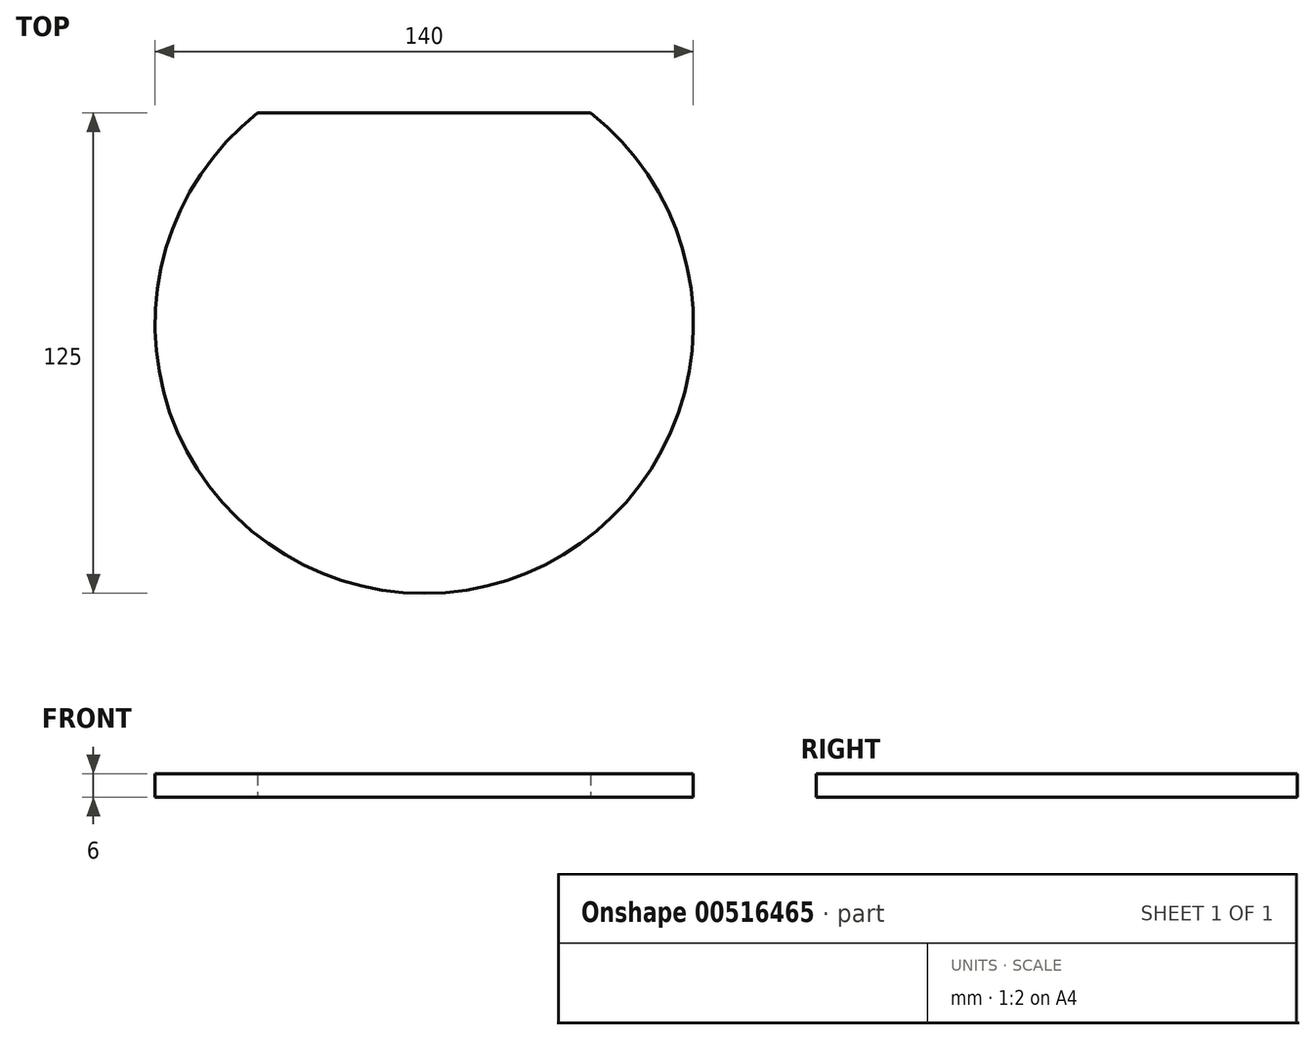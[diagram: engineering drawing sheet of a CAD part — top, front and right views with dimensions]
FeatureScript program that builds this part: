
annotation { "Feature Type Name" : "Feature", "Feature Type Description" : "" }
export const myFeature = defineFeature(function(context is Context, id is Id, definition is map)
    precondition{}
    {
        {
            var Q0;
            Q0=qCreatedBy(makeId("Top.planeOp"),FACE);
            var sketch = newSketch(context, id + "F0", { "sketchPlane" : qUnion([Q0])});
            skCircle(sketch, "E0", {"center": v(0, 0) * mm, "radius": 70 * mm});
            skSolve(sketch);
        }
        {
            var Q0;
            Q0=makeQuery(id+"F0.imprint","IMPRINT",FACE,{"disambiguationData":[TD([[makeQuery(id+"F0.imprint","IMPRINT",EDGE,{"derivedFrom":sQuery(id+"F0.wireOp",EDGE,"E0")}),1.0]])]});
            extrude(context, id + "F1", {"entities" : qUnion([Q0]), "oppositeDirection" : true, "depth" : 6 * mm, "offsetDistance" : 25 * mm});
        }
        {
            var Q0;
            Q0=makeQuery(id+"F1.opExtrude","CAP_FACE",FACE,{"disambiguationData":[OSD([sQuery(id+"F0.wireOp",EDGE,"E0")])],"isStart":true});
            var sketch = newSketch(context, id + "F2", { "sketchPlane" : qUnion([Q0])});
            skLineSegment(sketch, "E1", {"start": v(70, 0) * mm, "end": v(-70, 0) * mm});
            skLineSegment(sketch, "E2", {"start": v(-70, 0) * mm, "end": v(-35, 0) * mm});
            skCircle(sketch, "E3", {"center": v(-35, 0) * mm, "radius": 7 * mm});
            skSolve(sketch);
        }
        {
            var Q0;
            Q0=makeQuery(id+"F1.opExtrude","CAP_FACE",FACE,{"disambiguationData":[OSD([sQuery(id+"F0.wireOp",EDGE,"E0")])],"isStart":false});
            var sketch = newSketch(context, id + "F3", { "sketchPlane" : qUnion([Q0])});
            skLineSegment(sketch, "E4", {"start": v(0, 0) * mm, "end": v(0, -55) * mm});
            skLineSegment(sketch, "E5", {"start": v(0, -55) * mm, "end": v(-43.3, -55) * mm});
            skLineSegment(sketch, "E6", {"start": v(-43.3, -55) * mm, "end": v(43.3, -55) * mm});
            skSolve(sketch);
        }
        {
            var Q0;
            {var subQ0=sQuery(id+"F3.wireOp",EDGE,"E6");var subQ1=makeQuery(id+"F3.imprint","IMPRINT",VERTEX,{"derivedFrom":subQ0});Q0=makeQuery(id+"F3.imprint","IMPRINT",FACE,{"disambiguationData":[TD([[makeQuery(id+"F3.imprint","IMPRINT",EDGE,{"disambiguationData":[TD([[subQ1,1.0]])],"derivedFrom":subQ0}),-1.0]])]});}
            extrude(context, id + "F4", {"entities" : qUnion([Q0]), "operationType" : NewBodyOperationType.REMOVE, "oppositeDirection" : true, "depth" : 6 * mm, "offsetDistance" : 25 * mm});
        }
    });
